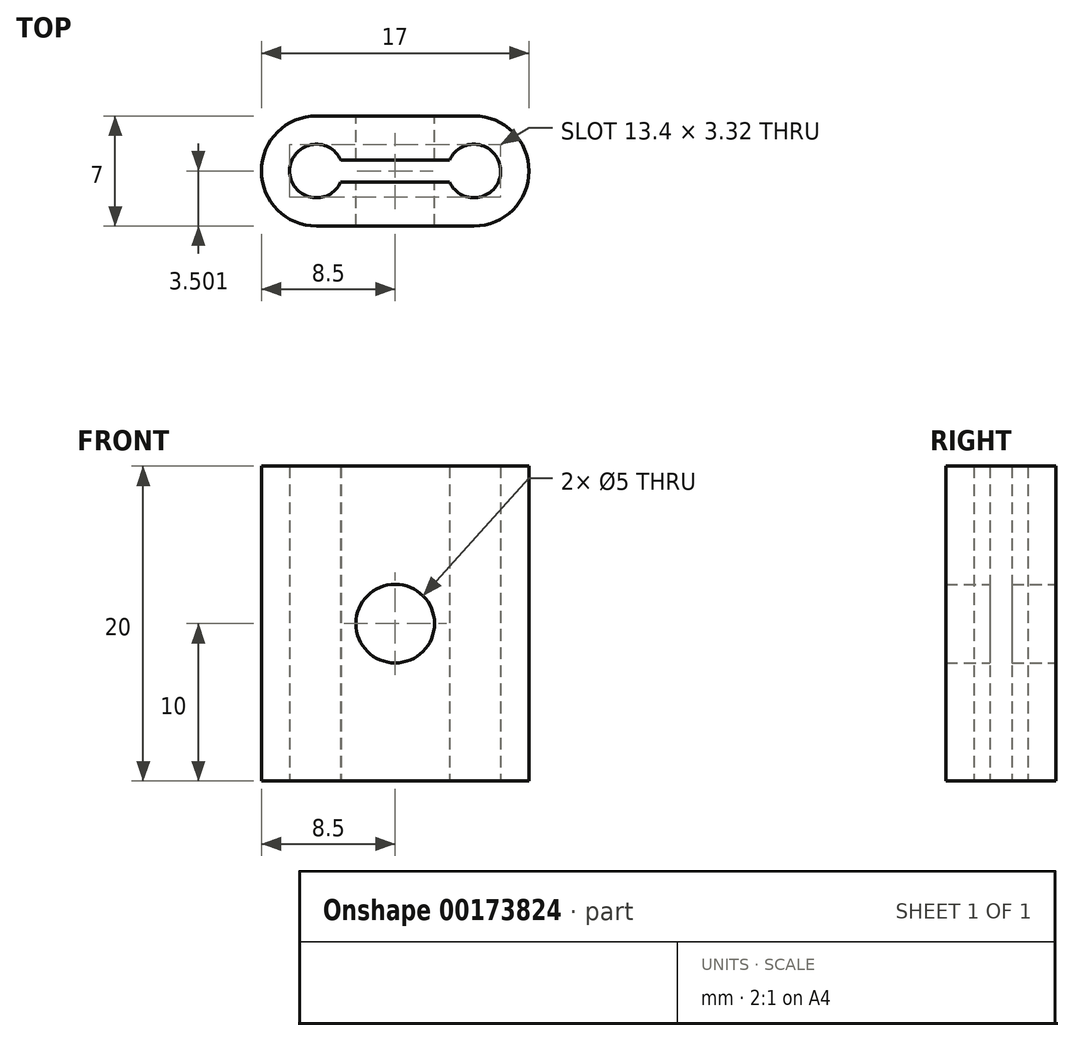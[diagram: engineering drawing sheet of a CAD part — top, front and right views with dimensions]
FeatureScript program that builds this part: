
annotation { "Feature Type Name" : "Feature", "Feature Type Description" : "" }
export const myFeature = defineFeature(function(context is Context, id is Id, definition is map)
    precondition{}
    {
        {
            var Q0;
            Q0=qCreatedBy(makeId("Top.planeOp"),FACE);
            var sketch = newSketch(context, id + "F0", { "sketchPlane" : qUnion([Q0])});
            skArc(sketch, "E0", {"start": v(3.46, -0.71) * mm, "mid": v(6.7, 0) * mm, "end": v(3.45, 0.7) * mm});
            skArc(sketch, "E1", {"start": v(5, -3.5) * mm, "mid": v(8.5, 0) * mm, "end": v(5, 3.5) * mm});
            skLineSegment(sketch, "E2", {"start": v(5, -3.5) * mm, "end": v(0, -3.5) * mm});
            skLineSegment(sketch, "E3", {"start": v(5, 3.5) * mm, "end": v(0, 3.5) * mm});
            skLineSegment(sketch, "E4", {"start": v(0, 0.7) * mm, "end": v(3.45, 0.7) * mm});
            skLineSegment(sketch, "E5", {"start": v(0, -0.71) * mm, "end": v(3.46, -0.71) * mm});
            skLineSegment(sketch, "E6", {"start": v(0, 3.5) * mm, "end": v(0, 0.7) * mm});
            skLineSegment(sketch, "E7", {"start": v(0, -0.71) * mm, "end": v(0, -3.5) * mm});
            skSolve(sketch);
        }
        {
            var Q0;
            Q0 = qSketchRegion(id + "F0", true);
            extrude(context, id + "F1", {"entities" : qUnion([Q0]), "depth" : 20 * mm, "offsetDistance" : 25 * mm});
        }
        {
            var Q0;
            Q0=makeQuery(id+"F1.opExtrude","SWEPT_BODY",BODY,{"disambiguationData":[OSD([sQuery(id+"F0.wireOp",EDGE,"E0"),sQuery(id+"F0.wireOp",EDGE,"E1"),sQuery(id+"F0.wireOp",EDGE,"E2"),sQuery(id+"F0.wireOp",EDGE,"E3"),sQuery(id+"F0.wireOp",EDGE,"E4"),sQuery(id+"F0.wireOp",EDGE,"E5"),sQuery(id+"F0.wireOp",EDGE,"E6"),sQuery(id+"F0.wireOp",EDGE,"E7")])]});
            var Q1;
            Q1=qCreatedBy(makeId("Right.planeOp"),FACE);
            mirror(context, id + "F2", {"operationType" : NewBodyOperationType.ADD, "entities" : qUnion([Q0]), "mirrorPlane" : qUnion([Q1])});
        }
        {
            var Q0;
            {var subQ0=makeQuery(id+"F1.opExtrude","SWEPT_FACE",FACE,{"disambiguationData":[OSD([sQuery(id+"F0.wireOp",EDGE,"E3")])]});Q0=makeQuery(id+"F2.boolean.opBoolean","MERGE",FACE,{"derivedFrom":[subQ0,makeQuery(id+"F2.opPattern","COPY",FACE,{"derivedFrom":subQ0,"instanceName":"1"})]});}
            var sketch = newSketch(context, id + "F3", { "sketchPlane" : qUnion([Q0])});
            skCircle(sketch, "E8", {"center": v(0, 10) * mm, "radius": 2.5 * mm});
            skSolve(sketch);
        }
        {
            var Q0;
            Q0=makeQuery(id+"F3.imprint","IMPRINT",FACE,{"disambiguationData":[TD([[makeQuery(id+"F3.imprint","IMPRINT",EDGE,{"derivedFrom":sQuery(id+"F3.wireOp",EDGE,"E8")}),1.0]])]});
            extrude(context, id + "F4", {"entities" : qUnion([Q0]), "operationType" : NewBodyOperationType.REMOVE, "endBound" : BoundingType.THROUGH_ALL, "oppositeDirection" : true, "depth" : 25 * mm, "offsetDistance" : 25 * mm});
        }
    });
